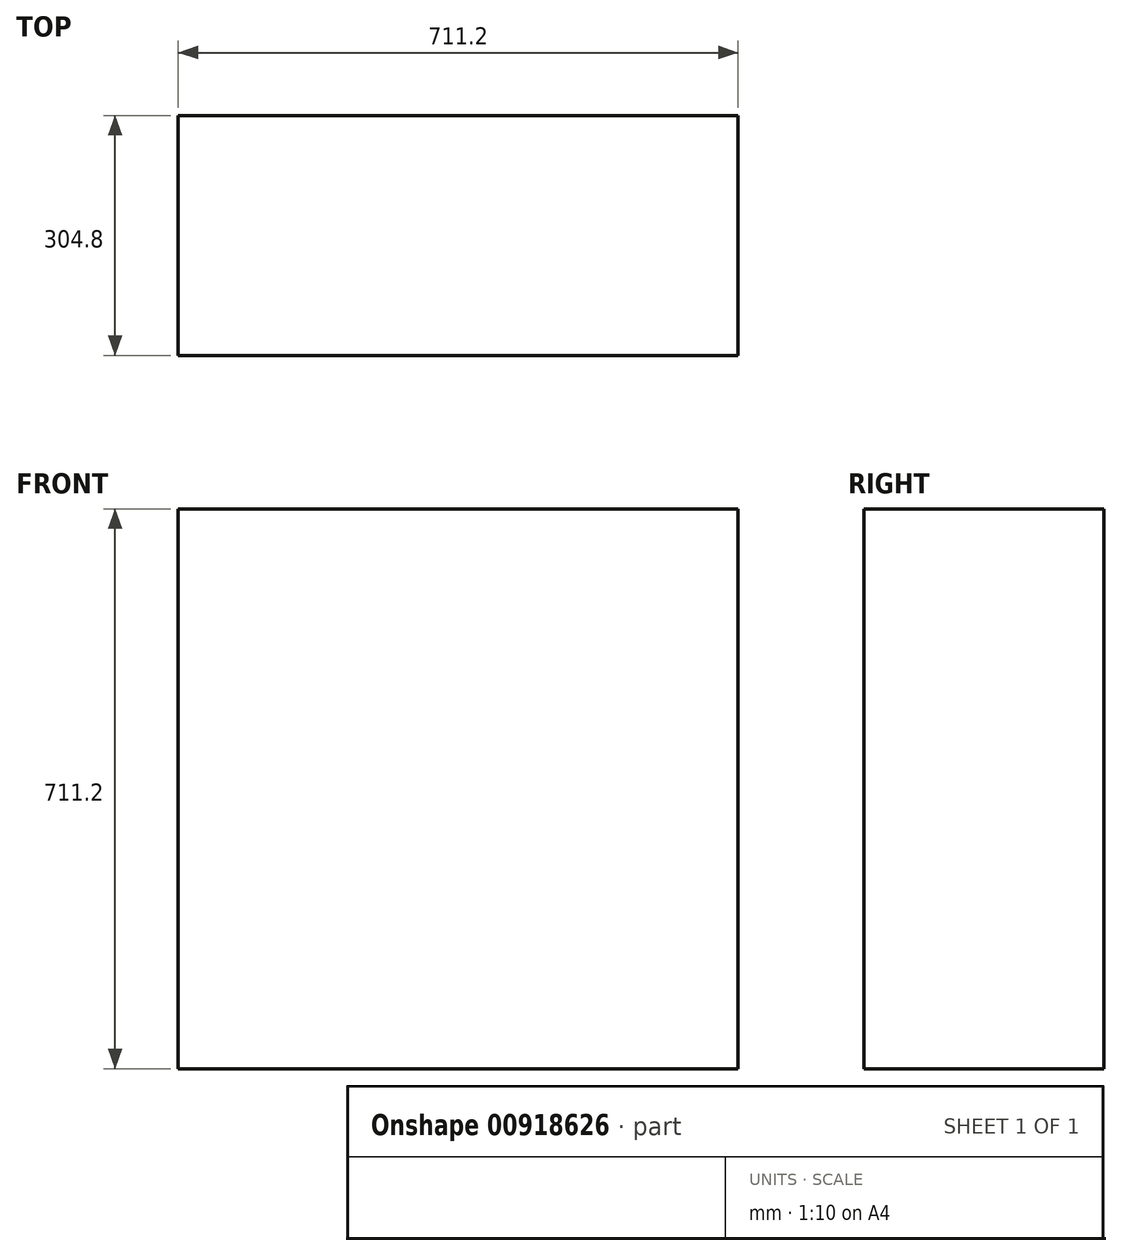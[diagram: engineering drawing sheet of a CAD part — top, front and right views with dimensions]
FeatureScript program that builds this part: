
annotation { "Feature Type Name" : "Feature", "Feature Type Description" : "" }
export const myFeature = defineFeature(function(context is Context, id is Id, definition is map)
    precondition{}
    {
        {
            var Q0;
            Q0=qCreatedBy(makeId("Front.planeOp"),FACE);
            var sketch = newSketch(context, id + "F0", { "sketchPlane" : qUnion([Q0])});
            skLineSegment(sketch, "E0.bottom", {"start": v(-355.6, 355.6) * mm, "end": v(355.6, 355.6) * mm});
            skLineSegment(sketch, "E0.top", {"start": v(-355.6, -355.6) * mm, "end": v(355.6, -355.6) * mm});
            skLineSegment(sketch, "E0.left", {"start": v(-355.6, 355.6) * mm, "end": v(-355.6, -355.6) * mm});
            skLineSegment(sketch, "E0.right", {"start": v(355.6, 355.6) * mm, "end": v(355.6, -355.6) * mm});
            skLineSegment(sketch, "E1", {"start": v(-355.6, 355.6) * mm, "end": v(355.6, -355.6) * mm, "construction": true});
            skSolve(sketch);
        }
        {
            var Q0;
            Q0=makeQuery(id+"F0.imprint","IMPRINT",FACE,{"disambiguationData":[TD([[makeQuery(id+"F0.imprint","IMPRINT",EDGE,{"derivedFrom":sQuery(id+"F0.wireOp",EDGE,"E0.bottom")}),-1.0]])]});
            extrude(context, id + "F1", {"entities" : qUnion([Q0]), "depth" : 304.8 * mm, "offsetDistance" : 25.4 * mm});
        }
    });
